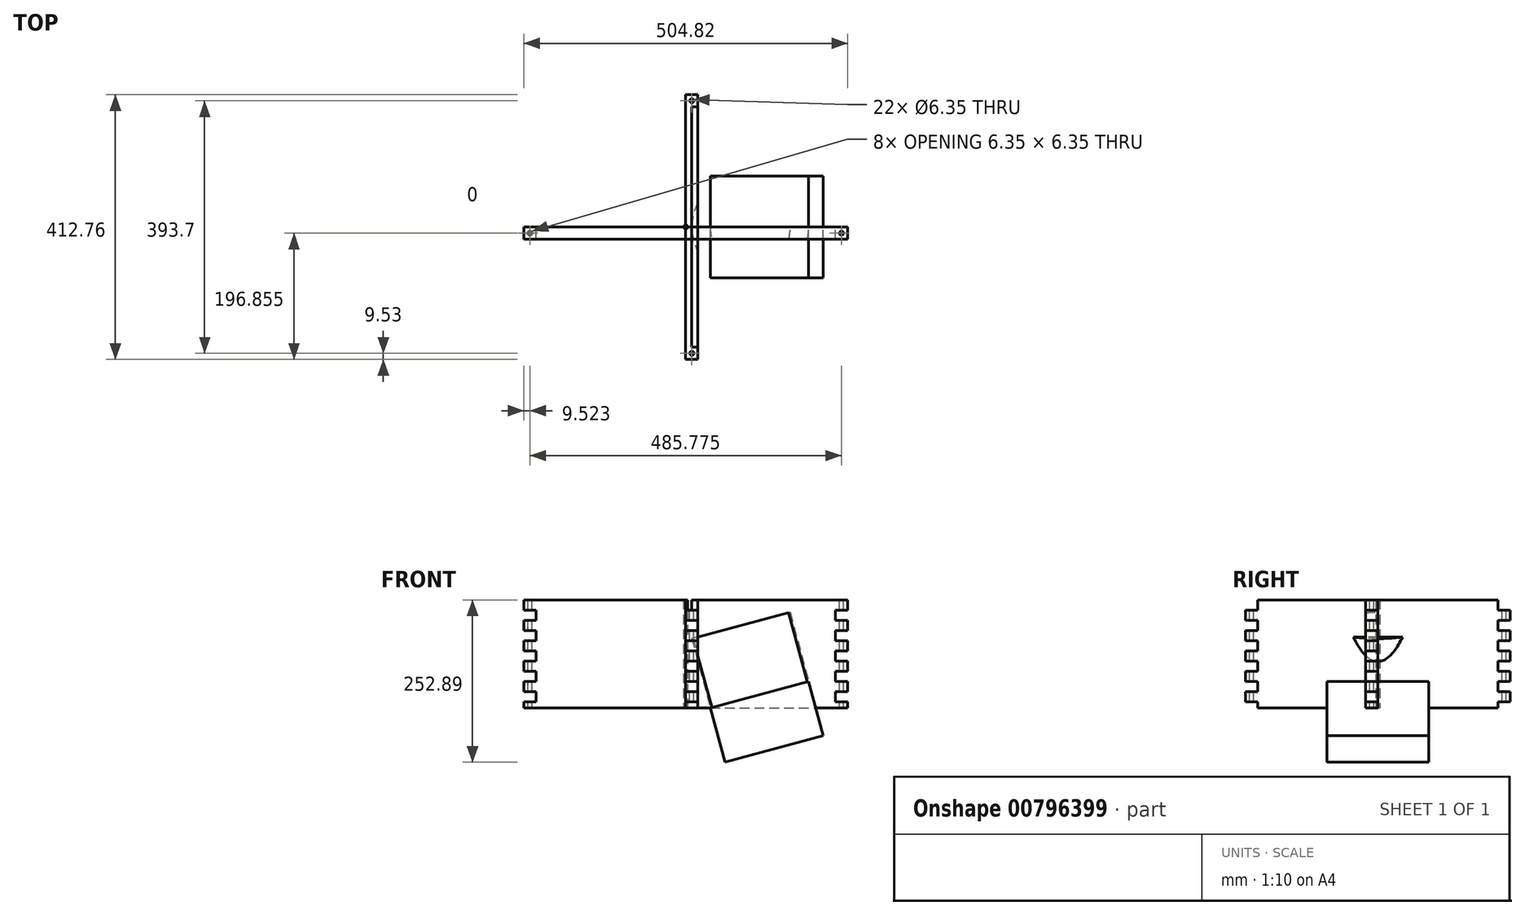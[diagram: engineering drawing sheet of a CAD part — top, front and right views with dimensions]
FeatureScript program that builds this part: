
annotation { "Feature Type Name" : "Feature", "Feature Type Description" : "" }
export const myFeature = defineFeature(function(context is Context, id is Id, definition is map)
    precondition{}
    {
        {
            var Q0;
            Q0=qCreatedBy(makeId("Front.planeOp"),FACE);
            var sketch = newSketch(context, id + "F0", { "sketchPlane" : qUnion([Q0])});
            skLineSegment(sketch, "E0", {"start": v(0, 168.28) * mm, "end": v(252.41, 168.28) * mm});
            skLineSegment(sketch, "E1", {"start": v(252.41, 168.28) * mm, "end": v(252.41, 152.4) * mm});
            skLineSegment(sketch, "E2", {"start": v(252.41, 152.4) * mm, "end": v(233.36, 152.4) * mm});
            skLineSegment(sketch, "E3", {"start": v(233.36, 152.4) * mm, "end": v(233.36, 136.53) * mm});
            skLineSegment(sketch, "E4", {"start": v(233.36, 136.53) * mm, "end": v(252.41, 136.53) * mm});
            skLineSegment(sketch, "E5", {"start": v(252.41, 136.53) * mm, "end": v(252.41, 120.65) * mm});
            skLineSegment(sketch, "E6", {"start": v(252.41, 120.65) * mm, "end": v(233.36, 120.65) * mm});
            skLineSegment(sketch, "E7", {"start": v(233.36, 120.65) * mm, "end": v(233.36, 104.77) * mm});
            skLineSegment(sketch, "E8", {"start": v(233.36, 104.78) * mm, "end": v(252.41, 104.78) * mm});
            skLineSegment(sketch, "E9", {"start": v(252.41, 104.77) * mm, "end": v(252.41, 88.9) * mm});
            skLineSegment(sketch, "E10", {"start": v(252.41, 88.9) * mm, "end": v(233.36, 88.9) * mm});
            skLineSegment(sketch, "E11", {"start": v(233.36, 88.9) * mm, "end": v(233.36, 73.02) * mm});
            skLineSegment(sketch, "E12", {"start": v(233.36, 73.03) * mm, "end": v(252.41, 73.03) * mm});
            skLineSegment(sketch, "E13", {"start": v(252.41, 73.02) * mm, "end": v(252.41, 57.15) * mm});
            skLineSegment(sketch, "E14", {"start": v(252.41, 57.15) * mm, "end": v(233.36, 57.15) * mm});
            skLineSegment(sketch, "E15", {"start": v(233.36, 57.15) * mm, "end": v(233.36, 41.27) * mm});
            skLineSegment(sketch, "E16", {"start": v(233.36, 41.27) * mm, "end": v(252.41, 41.27) * mm});
            skLineSegment(sketch, "E17", {"start": v(252.41, 41.27) * mm, "end": v(252.41, 25.4) * mm});
            skLineSegment(sketch, "E18", {"start": v(252.41, 25.4) * mm, "end": v(233.36, 25.4) * mm});
            skLineSegment(sketch, "E19", {"start": v(233.36, 25.4) * mm, "end": v(233.36, 9.52) * mm});
            skLineSegment(sketch, "E20", {"start": v(233.36, 9.52) * mm, "end": v(252.41, 9.52) * mm});
            skLineSegment(sketch, "E21", {"start": v(252.41, 9.52) * mm, "end": v(252.41, 0) * mm});
            skLineSegment(sketch, "E22", {"start": v(252.41, 0) * mm, "end": v(0, 0) * mm});
            skLineSegment(sketch, "E23.MirrorCS", {"start": v(-252.41, 0) * mm, "end": v(0, 0) * mm});
            skLineSegment(sketch, "E24.MirrorCS", {"start": v(0, 168.28) * mm, "end": v(-252.41, 168.28) * mm});
            skLineSegment(sketch, "E25.MirrorCS", {"start": v(-252.41, 168.28) * mm, "end": v(-252.41, 152.4) * mm});
            skLineSegment(sketch, "E26.MirrorCS", {"start": v(-252.41, 152.4) * mm, "end": v(-233.36, 152.4) * mm});
            skLineSegment(sketch, "E27.MirrorCS", {"start": v(-233.36, 152.4) * mm, "end": v(-233.36, 136.53) * mm});
            skLineSegment(sketch, "E28.MirrorCS", {"start": v(-233.36, 136.52) * mm, "end": v(-252.41, 136.52) * mm});
            skLineSegment(sketch, "E29.MirrorCS", {"start": v(-252.41, 136.53) * mm, "end": v(-252.41, 120.65) * mm});
            skLineSegment(sketch, "E30.MirrorCS", {"start": v(-252.41, 120.65) * mm, "end": v(-233.36, 120.65) * mm});
            skLineSegment(sketch, "E31.MirrorCS", {"start": v(-233.36, 120.65) * mm, "end": v(-233.36, 104.77) * mm});
            skLineSegment(sketch, "E32.MirrorCS", {"start": v(-233.36, 104.77) * mm, "end": v(-252.41, 104.77) * mm});
            skLineSegment(sketch, "E33.MirrorCS", {"start": v(-252.41, 104.77) * mm, "end": v(-252.41, 88.9) * mm});
            skLineSegment(sketch, "E34.MirrorCS", {"start": v(-252.41, 88.9) * mm, "end": v(-233.36, 88.9) * mm});
            skLineSegment(sketch, "E35.MirrorCS", {"start": v(-233.36, 88.9) * mm, "end": v(-233.36, 73.02) * mm});
            skLineSegment(sketch, "E36.MirrorCS", {"start": v(-233.36, 73.02) * mm, "end": v(-252.41, 73.02) * mm});
            skLineSegment(sketch, "E37.MirrorCS", {"start": v(-252.41, 73.02) * mm, "end": v(-252.41, 57.15) * mm});
            skLineSegment(sketch, "E38.MirrorCS", {"start": v(-252.41, 57.15) * mm, "end": v(-233.36, 57.15) * mm});
            skLineSegment(sketch, "E39.MirrorCS", {"start": v(-233.36, 57.15) * mm, "end": v(-233.36, 41.27) * mm});
            skLineSegment(sketch, "E40.MirrorCS", {"start": v(-233.36, 41.27) * mm, "end": v(-252.41, 41.27) * mm});
            skLineSegment(sketch, "E41.MirrorCS", {"start": v(-252.41, 41.27) * mm, "end": v(-252.41, 25.4) * mm});
            skLineSegment(sketch, "E42.MirrorCS", {"start": v(-252.41, 25.4) * mm, "end": v(-233.36, 25.4) * mm});
            skLineSegment(sketch, "E43.MirrorCS", {"start": v(-233.36, 25.4) * mm, "end": v(-233.36, 9.52) * mm});
            skLineSegment(sketch, "E44.MirrorCS", {"start": v(-233.36, 9.52) * mm, "end": v(-252.41, 9.52) * mm});
            skLineSegment(sketch, "E45.MirrorCS", {"start": v(-252.41, 9.52) * mm, "end": v(-252.41, 0) * mm});
            skSolve(sketch);
        }
        {
            var Q0;
            Q0=makeQuery(id+"F0.imprint","IMPRINT",FACE,{"disambiguationData":[TD([[makeQuery(id+"F0.imprint","IMPRINT",EDGE,{"derivedFrom":sQuery(id+"F0.wireOp",EDGE,"E0")}),-1.0]])]});
            extrude(context, id + "F1", {"entities" : qUnion([Q0]), "depth" : 19.05 * mm, "offsetDistance" : 25.4 * mm});
        }
        {
            var Q0;
            Q0=qCreatedBy(makeId("Right.planeOp"),FACE);
            var sketch = newSketch(context, id + "F2", { "sketchPlane" : qUnion([Q0])});
            skLineSegment(sketch, "E46", {"start": v(0, 168.28) * mm, "end": v(187.33, 168.28) * mm});
            skLineSegment(sketch, "E47", {"start": v(187.33, 168.28) * mm, "end": v(187.33, 152.4) * mm});
            skLineSegment(sketch, "E48", {"start": v(187.33, 152.4) * mm, "end": v(206.38, 152.4) * mm});
            skLineSegment(sketch, "E49", {"start": v(206.38, 152.4) * mm, "end": v(206.38, 136.52) * mm});
            skLineSegment(sketch, "E50", {"start": v(206.38, 136.53) * mm, "end": v(187.33, 136.52) * mm});
            skLineSegment(sketch, "E51", {"start": v(187.33, 136.52) * mm, "end": v(187.33, 120.65) * mm});
            skLineSegment(sketch, "E52", {"start": v(187.33, 120.65) * mm, "end": v(206.38, 120.65) * mm});
            skLineSegment(sketch, "E53", {"start": v(206.38, 120.65) * mm, "end": v(206.38, 104.77) * mm});
            skLineSegment(sketch, "E54", {"start": v(206.38, 104.77) * mm, "end": v(187.33, 104.77) * mm});
            skLineSegment(sketch, "E55", {"start": v(187.33, 104.77) * mm, "end": v(187.33, 88.9) * mm});
            skLineSegment(sketch, "E56", {"start": v(187.33, 88.9) * mm, "end": v(206.38, 88.9) * mm});
            skLineSegment(sketch, "E57", {"start": v(206.38, 88.9) * mm, "end": v(206.38, 73.02) * mm});
            skLineSegment(sketch, "E58", {"start": v(206.38, 73.02) * mm, "end": v(187.33, 73.02) * mm});
            skLineSegment(sketch, "E59", {"start": v(187.33, 73.02) * mm, "end": v(187.33, 57.15) * mm});
            skLineSegment(sketch, "E60", {"start": v(187.33, 57.15) * mm, "end": v(206.38, 57.15) * mm});
            skLineSegment(sketch, "E61", {"start": v(206.38, 57.15) * mm, "end": v(206.38, 41.27) * mm});
            skLineSegment(sketch, "E62", {"start": v(206.38, 41.27) * mm, "end": v(187.33, 41.27) * mm});
            skLineSegment(sketch, "E63", {"start": v(187.33, 41.27) * mm, "end": v(187.33, 25.4) * mm});
            skLineSegment(sketch, "E64", {"start": v(187.33, 25.4) * mm, "end": v(206.38, 25.4) * mm});
            skLineSegment(sketch, "E65", {"start": v(206.38, 25.4) * mm, "end": v(206.38, 9.52) * mm});
            skLineSegment(sketch, "E66", {"start": v(206.38, 9.52) * mm, "end": v(187.33, 9.52) * mm});
            skLineSegment(sketch, "E67", {"start": v(187.33, 9.52) * mm, "end": v(187.33, 0) * mm});
            skLineSegment(sketch, "E68", {"start": v(187.33, 0) * mm, "end": v(0, 0) * mm});
            skLineSegment(sketch, "E69.MirrorCS", {"start": v(0, 168.28) * mm, "end": v(-187.33, 168.28) * mm});
            skLineSegment(sketch, "E70.MirrorCS", {"start": v(-187.33, 0) * mm, "end": v(0, 0) * mm});
            skLineSegment(sketch, "E71.MirrorCS", {"start": v(-187.33, 152.4) * mm, "end": v(-206.38, 152.4) * mm});
            skLineSegment(sketch, "E72.MirrorCS", {"start": v(-206.38, 152.4) * mm, "end": v(-206.38, 136.52) * mm});
            skLineSegment(sketch, "E73.MirrorCS", {"start": v(-206.38, 136.52) * mm, "end": v(-187.33, 136.52) * mm});
            skLineSegment(sketch, "E74.MirrorCS", {"start": v(-187.33, 136.52) * mm, "end": v(-187.33, 120.65) * mm});
            skLineSegment(sketch, "E75.MirrorCS", {"start": v(-187.33, 120.65) * mm, "end": v(-206.38, 120.65) * mm});
            skLineSegment(sketch, "E76.MirrorCS", {"start": v(-206.38, 120.65) * mm, "end": v(-206.38, 104.77) * mm});
            skLineSegment(sketch, "E77.MirrorCS", {"start": v(-206.38, 104.77) * mm, "end": v(-187.33, 104.77) * mm});
            skLineSegment(sketch, "E78.MirrorCS", {"start": v(-187.33, 104.77) * mm, "end": v(-187.33, 88.9) * mm});
            skLineSegment(sketch, "E79.MirrorCS", {"start": v(-187.33, 88.9) * mm, "end": v(-206.38, 88.9) * mm});
            skLineSegment(sketch, "E80.MirrorCS", {"start": v(-206.38, 88.9) * mm, "end": v(-206.38, 73.02) * mm});
            skLineSegment(sketch, "E81.MirrorCS", {"start": v(-206.38, 73.02) * mm, "end": v(-187.33, 73.02) * mm});
            skLineSegment(sketch, "E82.MirrorCS", {"start": v(-187.33, 73.02) * mm, "end": v(-187.33, 57.15) * mm});
            skLineSegment(sketch, "E83.MirrorCS", {"start": v(-187.33, 57.15) * mm, "end": v(-206.38, 57.15) * mm});
            skLineSegment(sketch, "E84.MirrorCS", {"start": v(-206.38, 57.15) * mm, "end": v(-206.38, 41.27) * mm});
            skLineSegment(sketch, "E85.MirrorCS", {"start": v(-206.38, 41.27) * mm, "end": v(-187.33, 41.27) * mm});
            skLineSegment(sketch, "E86.MirrorCS", {"start": v(-187.33, 41.27) * mm, "end": v(-187.33, 25.4) * mm});
            skLineSegment(sketch, "E87.MirrorCS", {"start": v(-187.33, 25.4) * mm, "end": v(-206.38, 25.4) * mm});
            skLineSegment(sketch, "E88.MirrorCS", {"start": v(-206.38, 25.4) * mm, "end": v(-206.38, 9.52) * mm});
            skLineSegment(sketch, "E89.MirrorCS", {"start": v(-206.38, 9.52) * mm, "end": v(-187.33, 9.52) * mm});
            skLineSegment(sketch, "E90.MirrorCS", {"start": v(-187.33, 9.52) * mm, "end": v(-187.33, 0) * mm});
            skLineSegment(sketch, "E91.MirrorCS", {"start": v(-187.33, 168.28) * mm, "end": v(-187.33, 152.4) * mm});
            skSolve(sketch);
        }
        {
            var Q0;
            Q0=qSketchRegion(id+"F2",true);
            extrude(context, id + "F3", {"entities" : qUnion([Q0]), "depth" : 19.05 * mm, "offsetDistance" : 25.4 * mm});
        }
        {
            var Q0;
            Q0=makeQuery(id+"F3.opExtrude","SWEPT_FACE",FACE,{"disambiguationData":[OSD([sQuery(id+"F2.wireOp",EDGE,"E91.MirrorCS")])]});
            var sketch = newSketch(context, id + "F4", { "sketchPlane" : qUnion([Q0])});
            skLineSegment(sketch, "E92.bottom", {"start": v(0, 168.28) * mm, "end": v(9.53, 168.28) * mm});
            skLineSegment(sketch, "E92.top", {"start": v(0, 152.4) * mm, "end": v(9.53, 152.4) * mm});
            skLineSegment(sketch, "E92.left", {"start": v(0, 168.28) * mm, "end": v(0, 152.4) * mm});
            skLineSegment(sketch, "E92.right", {"start": v(9.53, 168.28) * mm, "end": v(9.53, 152.4) * mm});
            skSolve(sketch);
        }
        {
            var Q0;
            Q0=qSketchRegion(id+"F4",true);
            extrude(context, id + "F5", {"entities" : qUnion([Q0]), "operationType" : NewBodyOperationType.REMOVE, "oppositeDirection" : true, "depth" : 381 * mm, "offsetDistance" : 25.4 * mm});
        }
        {
            var Q0;
            Q0=makeQuery(id+"F5.boolean.opBoolean","MERGE",FACE,{"derivedFrom":[makeQuery(id+"F3.opExtrude","SWEPT_FACE",FACE,{"disambiguationData":[OSD([sQuery(id+"F2.wireOp",EDGE,"E48")])]}),makeQuery(id+"F3.opExtrude","SWEPT_FACE",FACE,{"disambiguationData":[OSD([sQuery(id+"F2.wireOp",EDGE,"E71.MirrorCS")])]}),makeQuery(id+"F5.opExtrude","SWEPT_FACE",FACE,{"disambiguationData":[OSD([sQuery(id+"F4.wireOp",EDGE,"E92.top")])]})]});
            var sketch = newSketch(context, id + "F6", { "sketchPlane" : qUnion([Q0])});
            skCircle(sketch, "E93", {"center": v(9.53, 196.85) * mm, "radius": 3.18 * mm});
            skCircle(sketch, "E94.MirrorC", {"center": v(9.53, -196.85) * mm, "radius": 3.18 * mm});
            skSolve(sketch);
        }
        {
            var Q0;
            Q0=qSketchRegion(id+"F6",true);
            extrude(context, id + "F7", {"entities" : qUnion([Q0]), "operationType" : NewBodyOperationType.REMOVE, "oppositeDirection" : true, "depth" : 152.4 * mm, "offsetDistance" : 25.4 * mm});
        }
        {
            var Q0;
            Q0=makeQuery(id+"F1.opExtrude","SWEPT_FACE",FACE,{"disambiguationData":[OSD([sQuery(id+"F0.wireOp",EDGE,"E0"),sQuery(id+"F0.wireOp",EDGE,"E24.MirrorCS")])]});
            var sketch = newSketch(context, id + "F8", { "sketchPlane" : qUnion([Q0])});
            skCircle(sketch, "E95", {"center": v(-242.89, -9.53) * mm, "radius": 3.18 * mm});
            skCircle(sketch, "E96.MirrorC", {"center": v(242.89, -9.53) * mm, "radius": 3.18 * mm});
            skSolve(sketch);
        }
        {
            var Q0;
            Q0=qSketchRegion(id+"F8",true);
            extrude(context, id + "F9", {"entities" : qUnion([Q0]), "operationType" : NewBodyOperationType.REMOVE, "oppositeDirection" : true, "depth" : 177.8 * mm, "offsetDistance" : 25.4 * mm});
        }
        {
            var Q0;
            Q0=qCreatedBy(makeId("Top.planeOp"),FACE);
            var sketch = newSketch(context, id + "F10", { "sketchPlane" : qUnion([Q0])});
            skCircle(sketch, "E97", {"center": v(0, 0) * mm, "radius": 3.18 * mm});
            skSolve(sketch);
        }
        {
            var Q0;
            Q0=makeQuery(id+"F10.imprint","IMPRINT",FACE,{"disambiguationData":[TD([[makeQuery(id+"F10.imprint","IMPRINT",EDGE,{"derivedFrom":sQuery(id+"F10.wireOp",EDGE,"E97")}),1.0]])]});
            extrude(context, id + "F11", {"entities" : qUnion([Q0]), "depth" : 168.27 * mm, "offsetDistance" : 25.4 * mm});
        }
        {
            var Q0;
            Q0=qCreatedBy(makeId("Front.planeOp"),FACE);
            var sketch = newSketch(context, id + "F12", { "sketchPlane" : qUnion([Q0])});
            skLineSegment(sketch, "E98", {"start": v(38.45, 0) * mm, "end": v(61.12, -84.6) * mm});
            skLineSegment(sketch, "E99", {"start": v(38.45, 0) * mm, "end": v(191.8, 41.09) * mm});
            skLineSegment(sketch, "E100", {"start": v(191.8, 41.09) * mm, "end": v(214.46, -43.52) * mm});
            skLineSegment(sketch, "E101", {"start": v(214.46, -43.52) * mm, "end": v(61.12, -84.6) * mm});
            skSolve(sketch);
        }
        {
            var Q0;
            Q0=makeQuery(id+"F12.imprint","IMPRINT",FACE,{"disambiguationData":[TD([[makeQuery(id+"F12.imprint","IMPRINT",EDGE,{"derivedFrom":sQuery(id+"F12.wireOp",EDGE,"E98")}),1.0]])]});
            extrude(context, id + "F13", {"entities" : qUnion([Q0]), "depth" : 158.75 * mm, "offsetDistance" : 25.4 * mm, "symmetric" : true});
        }
        {
            var Q0;
            Q0=makeQuery(id+"F13.opExtrude","SWEPT_FACE",FACE,{"disambiguationData":[OSD([sQuery(id+"F12.wireOp",EDGE,"E99")])]});
            var sketch = newSketch(context, id + "F14", { "sketchPlane" : qUnion([Q0])});
            skCircle(sketch, "E102", {"center": v(116.51, 0) * mm, "radius": 79.38 * mm});
            skSolve(sketch);
        }
        {
            var Q0;
            {var subQ0=sQuery(id+"F14.wireOp",EDGE,"E102");var subQ1=sQuery(id+"F12.wireOp",EDGE,"E99");var subQ2=makeQuery(id+"F14.imprint","INTERSECT",VERTEX,{"derivedFrom":[makeQuery(id+"F13.opExtrude","CAP_EDGE",EDGE,{"disambiguationData":[OSD([subQ1])],"isStart":true}),subQ0]});Q0=makeQuery(id+"F14.imprint","IMPRINT",FACE,{"disambiguationData":[TD([[makeQuery(id+"F14.imprint","IMPRINT",EDGE,{"disambiguationData":[TD([[subQ2,1.0]])],"derivedFrom":subQ0}),1.0]])]});}
            extrude(context, id + "F15", {"entities" : qUnion([Q0]), "operationType" : NewBodyOperationType.REMOVE, "depth" : 111.76 * mm, "offsetDistance" : 25.4 * mm});
        }
    });
